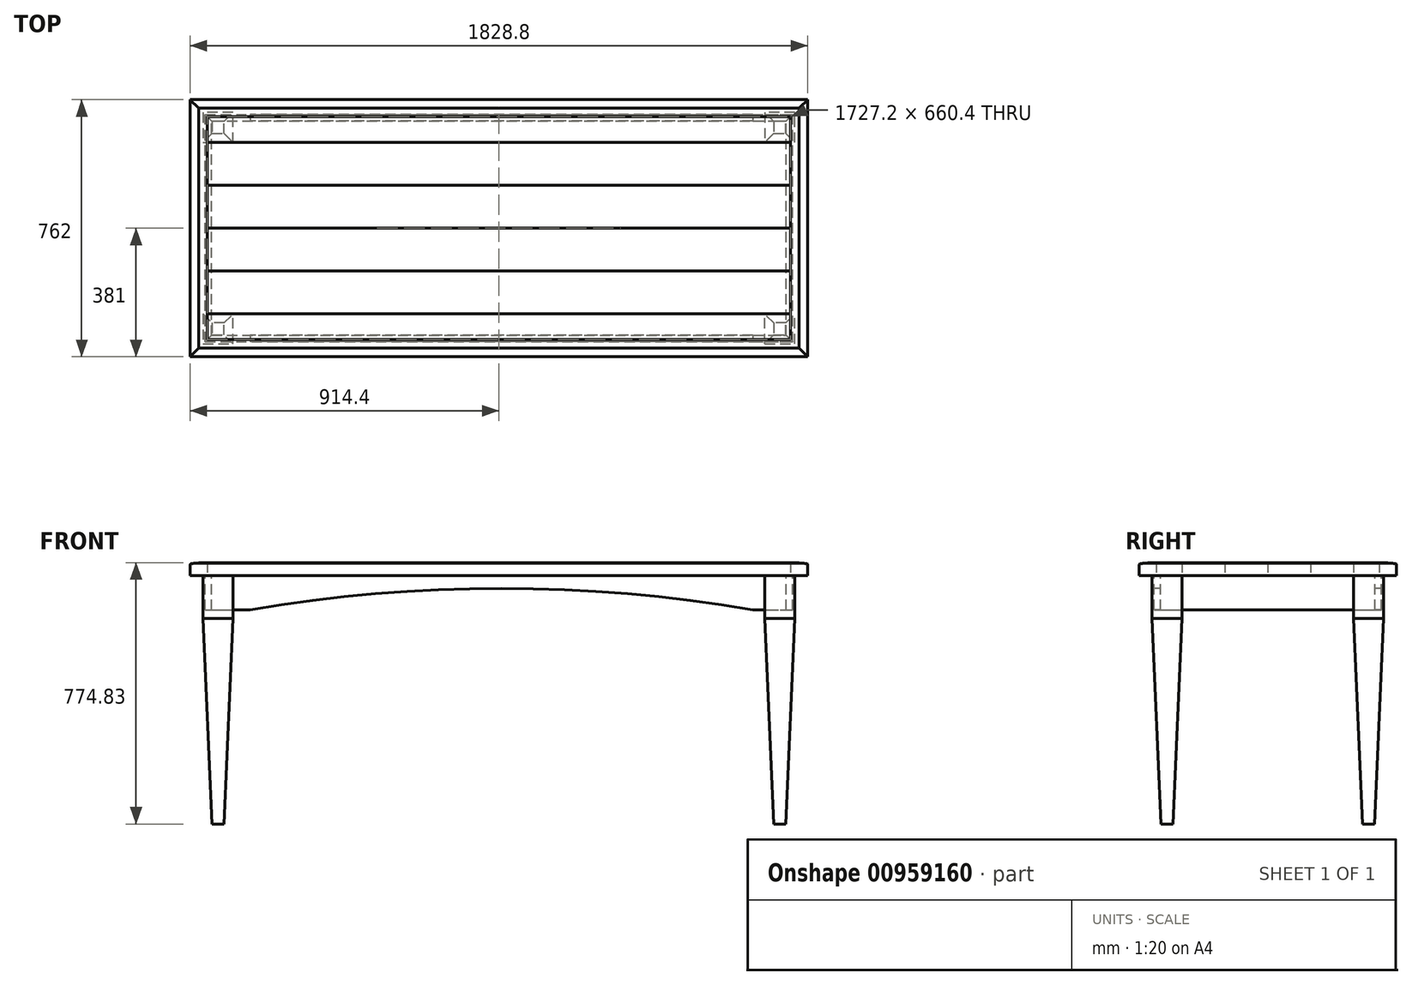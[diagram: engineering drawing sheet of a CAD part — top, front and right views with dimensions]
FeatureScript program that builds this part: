
annotation { "Feature Type Name" : "Feature", "Feature Type Description" : "" }
export const myFeature = defineFeature(function(context is Context, id is Id, definition is map)
    precondition{}
    {
        {
            var Q0;
            Q0=qCreatedBy(makeId("Top.planeOp"),FACE);
            var sketch = newSketch(context, id + "F0", { "sketchPlane" : qUnion([Q0])});
            skLineSegment(sketch, "E0.bottom", {"start": v(-863.6, 330.2) * mm, "end": v(863.6, 330.2) * mm});
            skLineSegment(sketch, "E0.top", {"start": v(-863.6, -330.2) * mm, "end": v(863.6, -330.2) * mm});
            skLineSegment(sketch, "E0.left", {"start": v(-863.6, 330.2) * mm, "end": v(-863.6, -330.2) * mm});
            skLineSegment(sketch, "E0.right", {"start": v(863.6, 330.2) * mm, "end": v(863.6, -330.2) * mm});
            skPoint(sketch, "E0.middle", {"position": v(0, 0) * mm});
            skLineSegment(sketch, "E1", {"start": v(-863.6, 254) * mm, "end": v(863.6, 254) * mm});
            skLineSegment(sketch, "E2.0.1.0", {"start": v(-863.6, 127) * mm, "end": v(863.6, 127) * mm});
            skLineSegment(sketch, "E2.0.2.0", {"start": v(-863.6, 0) * mm, "end": v(863.6, 0) * mm});
            skLineSegment(sketch, "E2.0.3.0", {"start": v(-863.6, -127) * mm, "end": v(863.6, -127) * mm});
            skLineSegment(sketch, "E2.0.4.0", {"start": v(-863.6, -254) * mm, "end": v(863.6, -254) * mm});
            skLineSegment(sketch, "E2.direction1", {"start": v(-863.6, 254) * mm, "end": v(-863.6, 254) * mm});
            skLineSegment(sketch, "E2.direction2", {"start": v(-863.6, 254) * mm, "end": v(-863.6, 127) * mm, "construction": true});
            skSolve(sketch);
        }
        {
            var Q0;
            {var subQ0=sQuery(id+"F0.wireOp",EDGE,"E0.bottom");Q0=makeQuery(id+"F0.imprint","IMPRINT",FACE,{"disambiguationData":[TD([[makeQuery(id+"F0.imprint","IMPRINT",EDGE,{"derivedFrom":subQ0}),-1.0]])]});}
            var Q1;
            {var subQ0=sQuery(id+"F0.wireOp",EDGE,"E2.0.1.0");Q1=makeQuery(id+"F0.imprint","IMPRINT",FACE,{"disambiguationData":[TD([[makeQuery(id+"F0.imprint","IMPRINT",EDGE,{"derivedFrom":subQ0}),-1.0]])]});}
            var Q2;
            {var subQ0=sQuery(id+"F0.wireOp",EDGE,"E2.0.3.0");Q2=makeQuery(id+"F0.imprint","IMPRINT",FACE,{"disambiguationData":[TD([[makeQuery(id+"F0.imprint","IMPRINT",EDGE,{"derivedFrom":subQ0}),-1.0]])]});}
            extrude(context, id + "F1", {"entities" : qUnion([Q0, Q1, Q2]), "depth" : 38.1 * mm, "offsetDistance" : 25.4 * mm});
        }
        {
            var Q0;
            {var subQ0=sQuery(id+"F0.wireOp",EDGE,"E1");Q0=makeQuery(id+"F0.imprint","IMPRINT",FACE,{"disambiguationData":[TD([[makeQuery(id+"F0.imprint","IMPRINT",EDGE,{"derivedFrom":subQ0}),-1.0]])]});}
            var Q1;
            {var subQ0=sQuery(id+"F0.wireOp",EDGE,"E2.0.2.0");Q1=makeQuery(id+"F0.imprint","IMPRINT",FACE,{"disambiguationData":[TD([[makeQuery(id+"F0.imprint","IMPRINT",EDGE,{"derivedFrom":subQ0}),-1.0]])]});}
            var Q2;
            {var subQ0=sQuery(id+"F0.wireOp",EDGE,"E0.top");Q2=makeQuery(id+"F0.imprint","IMPRINT",FACE,{"disambiguationData":[TD([[makeQuery(id+"F0.imprint","IMPRINT",EDGE,{"derivedFrom":subQ0}),1.0]])]});}
            extrude(context, id + "F2", {"entities" : qUnion([Q0, Q1, Q2]), "depth" : 38.23 * mm, "offsetDistance" : 25.4 * mm});
        }
        {
            var Q0;
            Q0=qCreatedBy(makeId("Right.planeOp"),FACE);
            var sketch = newSketch(context, id + "F3", { "sketchPlane" : qUnion([Q0])});
            skLineSegment(sketch, "E3", {"start": v(-329.63, 0) * mm, "end": v(-381, 0) * mm});
            skLineSegment(sketch, "E4", {"start": v(-147, 139.44) * mm, "end": v(-147, 139.44) * mm});
            skLineSegment(sketch, "E5", {"start": v(-140.65, 145.8) * mm, "end": v(-140.65, 145.8) * mm});
            skLineSegment(sketch, "E6", {"start": v(-355.6, 38.1) * mm, "end": v(-330.2, 38.1) * mm});
            skPoint(sketch, "E7.visualSharp", {"position": v(-396.17, 38.1) * mm});
            skPoint(sketch, "E8.visualSharp", {"position": v(-396.17, 6.35) * mm});
            skLineSegment(sketch, "E9", {"start": v(-330.2, 38.1) * mm, "end": v(-330.2, 0) * mm});
            skLineSegment(sketch, "E10", {"start": v(-355.6, 38.1) * mm, "end": v(-355.6, 36.51) * mm});
            skLineSegment(sketch, "E11", {"start": v(-381, 0) * mm, "end": v(-381, 28.58) * mm});
            skFitSpline(sketch, "E12", {"points": [v(-355.6, 36.51) * mm, v(-377.44, 35.2) * mm, v(-381, 28.58) * mm], "startDerivative": vector(-24.67, 0) * mm, "endDerivative": vector(0, -43.23) * mm});
            skLineSegment(sketch, "E13", {"start": v(-358.08, 36.51) * mm, "end": v(-355.6, 36.51) * mm, "construction": true});
            skSolve(sketch);
        }
        {
            var Q0;
            Q0=makeQuery(id+"F3.imprint","IMPRINT",FACE,{"disambiguationData":[TD([[makeQuery(id+"F3.imprint","IMPRINT",EDGE,{"derivedFrom":sQuery(id+"F3.wireOp",EDGE,"E6")}),-1.0]])]});
            var Q1;
            Q1=sQuery(id+"F0.wireOp",EDGE,"E0.top");
            var Q2;
            Q2=sQuery(id+"F0.wireOp",EDGE,"E0.right");
            var Q3;
            Q3=sQuery(id+"F0.wireOp",EDGE,"E0.bottom");
            var Q4;
            Q4=sQuery(id+"F0.wireOp",EDGE,"E0.left");
            sweep(context, id + "F4", {"profiles" : qUnion([Q0]), "path" : qUnion([Q1, Q2, Q3, Q4])});
        }
        {
            var Q0;
            Q0=qCreatedBy(makeId("Top.planeOp"),FACE);
            var sketch = newSketch(context, id + "F5", { "sketchPlane" : qUnion([Q0])});
            skLineSegment(sketch, "E14.bottom", {"start": v(-787.4, -342.9) * mm, "end": v(-876.3, -342.9) * mm});
            skLineSegment(sketch, "E14.top", {"start": v(-787.4, -254) * mm, "end": v(-876.3, -254) * mm});
            skLineSegment(sketch, "E14.left", {"start": v(-787.4, -342.9) * mm, "end": v(-787.4, -254) * mm});
            skLineSegment(sketch, "E14.right", {"start": v(-876.3, -342.9) * mm, "end": v(-876.3, -254) * mm});
            skPoint(sketch, "E14.middle", {"position": v(-831.85, -298.45) * mm});
            skLineSegment(sketch, "E15.MirrorCS", {"start": v(787.4, -342.9) * mm, "end": v(787.4, -254) * mm});
            skLineSegment(sketch, "E16.MirrorCS", {"start": v(787.4, -342.9) * mm, "end": v(876.3, -342.9) * mm});
            skLineSegment(sketch, "E17.MirrorCS", {"start": v(876.3, -342.9) * mm, "end": v(876.3, -254) * mm});
            skLineSegment(sketch, "E18.MirrorCS", {"start": v(787.4, -254) * mm, "end": v(876.3, -254) * mm});
            skLineSegment(sketch, "E19.MirrorCS", {"start": v(787.4, 342.9) * mm, "end": v(876.3, 342.9) * mm});
            skLineSegment(sketch, "E20.MirrorCS", {"start": v(-787.4, 342.9) * mm, "end": v(-787.4, 254) * mm});
            skLineSegment(sketch, "E21.MirrorCS", {"start": v(787.4, 254) * mm, "end": v(876.3, 254) * mm});
            skLineSegment(sketch, "E22.MirrorCS", {"start": v(-876.3, 342.9) * mm, "end": v(-876.3, 254) * mm});
            skPoint(sketch, "E23.MirrorP", {"position": v(-831.85, 298.45) * mm});
            skLineSegment(sketch, "E24.MirrorCS", {"start": v(-787.4, 342.9) * mm, "end": v(-876.3, 342.9) * mm});
            skLineSegment(sketch, "E25.MirrorCS", {"start": v(-787.4, 254) * mm, "end": v(-876.3, 254) * mm});
            skLineSegment(sketch, "E26.MirrorCS", {"start": v(876.3, 342.9) * mm, "end": v(876.3, 254) * mm});
            skLineSegment(sketch, "E27.MirrorCS", {"start": v(787.4, 342.9) * mm, "end": v(787.4, 254) * mm});
            skSolve(sketch);
        }
        {
            var Q0;
            Q0=qSketchRegion(id+"F5",true);
            extrude(context, id + "F6", {"entities" : qUnion([Q0]), "oppositeDirection" : true, "depth" : 127 * mm, "offsetDistance" : 25.4 * mm});
        }
        {
            var Q0;
            Q0=qCreatedBy(makeId("Top.planeOp"),FACE);
            var sketch = newSketch(context, id + "F7", { "sketchPlane" : qUnion([Q0])});
            skLineSegment(sketch, "E28.bottom", {"start": v(-869.95, -336.55) * mm, "end": v(869.95, -336.55) * mm});
            skLineSegment(sketch, "E28.top", {"start": v(-869.95, 336.55) * mm, "end": v(869.95, 336.55) * mm});
            skLineSegment(sketch, "E28.left", {"start": v(-869.95, -336.55) * mm, "end": v(-869.95, 336.55) * mm});
            skLineSegment(sketch, "E28.right", {"start": v(869.95, -336.55) * mm, "end": v(869.95, 336.55) * mm});
            skPoint(sketch, "E28.middle", {"position": v(0, 0) * mm});
            skLineSegment(sketch, "E29.0", {"start": v(-850.9, -317.5) * mm, "end": v(850.9, -317.5) * mm});
            skLineSegment(sketch, "E29.1", {"start": v(-850.9, -317.5) * mm, "end": v(-850.9, 317.5) * mm});
            skLineSegment(sketch, "E29.2", {"start": v(-850.9, 317.5) * mm, "end": v(850.9, 317.5) * mm});
            skLineSegment(sketch, "E29.3", {"start": v(850.9, -317.5) * mm, "end": v(850.9, 317.5) * mm});
            skSolve(sketch);
        }
        {
            var Q0;
            Q0=qSketchRegion(id+"F7",true);
            extrude(context, id + "F8", {"entities" : qUnion([Q0]), "oppositeDirection" : true, "depth" : 101.6 * mm, "offsetDistance" : 25.4 * mm});
        }
        {
            var Q0;
            Q0=makeQuery(id+"F6.opExtrude","CAP_FACE",FACE,{"disambiguationData":[OSD([sQuery(id+"F5.wireOp",EDGE,"E14.bottom"),sQuery(id+"F5.wireOp",EDGE,"E14.top"),sQuery(id+"F5.wireOp",EDGE,"E14.left"),sQuery(id+"F5.wireOp",EDGE,"E14.right")])],"isStart":false});
            var sketch = newSketch(context, id + "F9", { "sketchPlane" : qUnion([Q0])});
            skLineSegment(sketch, "E30.0.0", {"start": v(-787.4, 254) * mm, "end": v(-787.4, 342.9) * mm});
            skLineSegment(sketch, "E30.0.1", {"start": v(-787.4, 342.9) * mm, "end": v(-876.3, 342.9) * mm});
            skLineSegment(sketch, "E30.0.2", {"start": v(-876.3, 342.9) * mm, "end": v(-876.3, 254) * mm});
            skLineSegment(sketch, "E30.0.3", {"start": v(-876.3, 254) * mm, "end": v(-787.4, 254) * mm});
            skLineSegment(sketch, "E31.0.0", {"start": v(787.4, 254) * mm, "end": v(876.3, 254) * mm});
            skLineSegment(sketch, "E31.0.1", {"start": v(876.3, 254) * mm, "end": v(876.3, 342.9) * mm});
            skLineSegment(sketch, "E31.0.2", {"start": v(876.3, 342.9) * mm, "end": v(787.4, 342.9) * mm});
            skLineSegment(sketch, "E31.0.3", {"start": v(787.4, 342.9) * mm, "end": v(787.4, 254) * mm});
            skLineSegment(sketch, "E32.0.0", {"start": v(787.4, -254) * mm, "end": v(787.4, -342.9) * mm});
            skLineSegment(sketch, "E32.0.1", {"start": v(787.4, -342.9) * mm, "end": v(876.3, -342.9) * mm});
            skLineSegment(sketch, "E32.0.2", {"start": v(876.3, -342.9) * mm, "end": v(876.3, -254) * mm});
            skLineSegment(sketch, "E32.0.3", {"start": v(876.3, -254) * mm, "end": v(787.4, -254) * mm});
            skLineSegment(sketch, "E33.0.0", {"start": v(-876.3, -342.9) * mm, "end": v(-787.4, -342.9) * mm});
            skLineSegment(sketch, "E33.0.1", {"start": v(-787.4, -342.9) * mm, "end": v(-787.4, -254) * mm});
            skLineSegment(sketch, "E33.0.2", {"start": v(-787.4, -254) * mm, "end": v(-876.3, -254) * mm});
            skLineSegment(sketch, "E33.0.3", {"start": v(-876.3, -254) * mm, "end": v(-876.3, -342.9) * mm});
            skSolve(sketch);
        }
        {
            var Q0;
            Q0=qSketchRegion(id+"F9",true);
            extrude(context, id + "F10", {"entities" : qUnion([Q0]), "depth" : 609.6 * mm, "offsetDistance" : 25.4 * mm, "hasDraft" : true, "draftAngle" : 2.5 * degree, "draftPullDirection" : true});
        }
        {
            var Q0;
            Q0=makeQuery(id+"F8.opExtrude","SWEPT_FACE",FACE,{"disambiguationData":[OSD([sQuery(id+"F7.wireOp",EDGE,"E28.bottom")])]});
            var sketch = newSketch(context, id + "F11", { "sketchPlane" : qUnion([Q0])});
            skLineSegment(sketch, "E34.0.0", {"start": v(-787.4, 0) * mm, "end": v(-876.3, 0) * mm, "construction": true});
            skLineSegment(sketch, "E34.0.1", {"start": v(-876.3, 0) * mm, "end": v(-876.3, -127) * mm, "construction": true});
            skLineSegment(sketch, "E34.0.2", {"start": v(-876.3, -127) * mm, "end": v(-787.4, -127) * mm, "construction": true});
            skLineSegment(sketch, "E34.0.3", {"start": v(-787.4, -127) * mm, "end": v(-787.4, 0) * mm, "construction": true});
            skLineSegment(sketch, "E35.0.0", {"start": v(869.95, 0) * mm, "end": v(-869.95, 0) * mm, "construction": true});
            skLineSegment(sketch, "E35.0.1", {"start": v(-869.95, 0) * mm, "end": v(-869.95, -101.6) * mm, "construction": true});
            skLineSegment(sketch, "E35.0.2", {"start": v(-869.95, -101.6) * mm, "end": v(869.95, -101.6) * mm, "construction": true});
            skLineSegment(sketch, "E35.0.3", {"start": v(869.95, -101.6) * mm, "end": v(869.95, 0) * mm});
            skLineSegment(sketch, "E36", {"start": v(-787.4, -101.6) * mm, "end": v(-736.6, -101.6) * mm, "construction": true});
            skArc(sketch, "E37", {"start": v(751.7, -101.6) * mm, "mid": v(7.55, -38.1) * mm, "end": v(-736.6, -101.6) * mm});
            skPoint(sketch, "E38", {"position": v(0, -38.1) * mm});
            skPoint(sketch, "E38.positionSnap0", {"position": v(0, -101.6) * mm});
            skLineSegment(sketch, "E39.bottom", {"start": v(-736.6, -101.6) * mm, "end": v(751.7, -101.6) * mm});
            skLineSegment(sketch, "E39.top", {"start": v(-736.6, -300.52) * mm, "end": v(751.7, -300.52) * mm});
            skLineSegment(sketch, "E39.left", {"start": v(-736.6, -101.6) * mm, "end": v(-736.6, -300.52) * mm});
            skLineSegment(sketch, "E39.right", {"start": v(751.7, -101.6) * mm, "end": v(751.7, -300.52) * mm});
            skSolve(sketch);
        }
        {
            var Q0;
            Q0=qSketchRegion(id+"F11",true);
            extrude(context, id + "F12", {"entities" : qUnion([Q0]), "operationType" : NewBodyOperationType.REMOVE, "oppositeDirection" : true, "depth" : 914.4 * mm, "offsetDistance" : 25.4 * mm, "hasSecondDirection" : true, "secondDirectionOppositeDirection" : false, "secondDirectionDepth" : 914.4 * mm});
        }
    });
